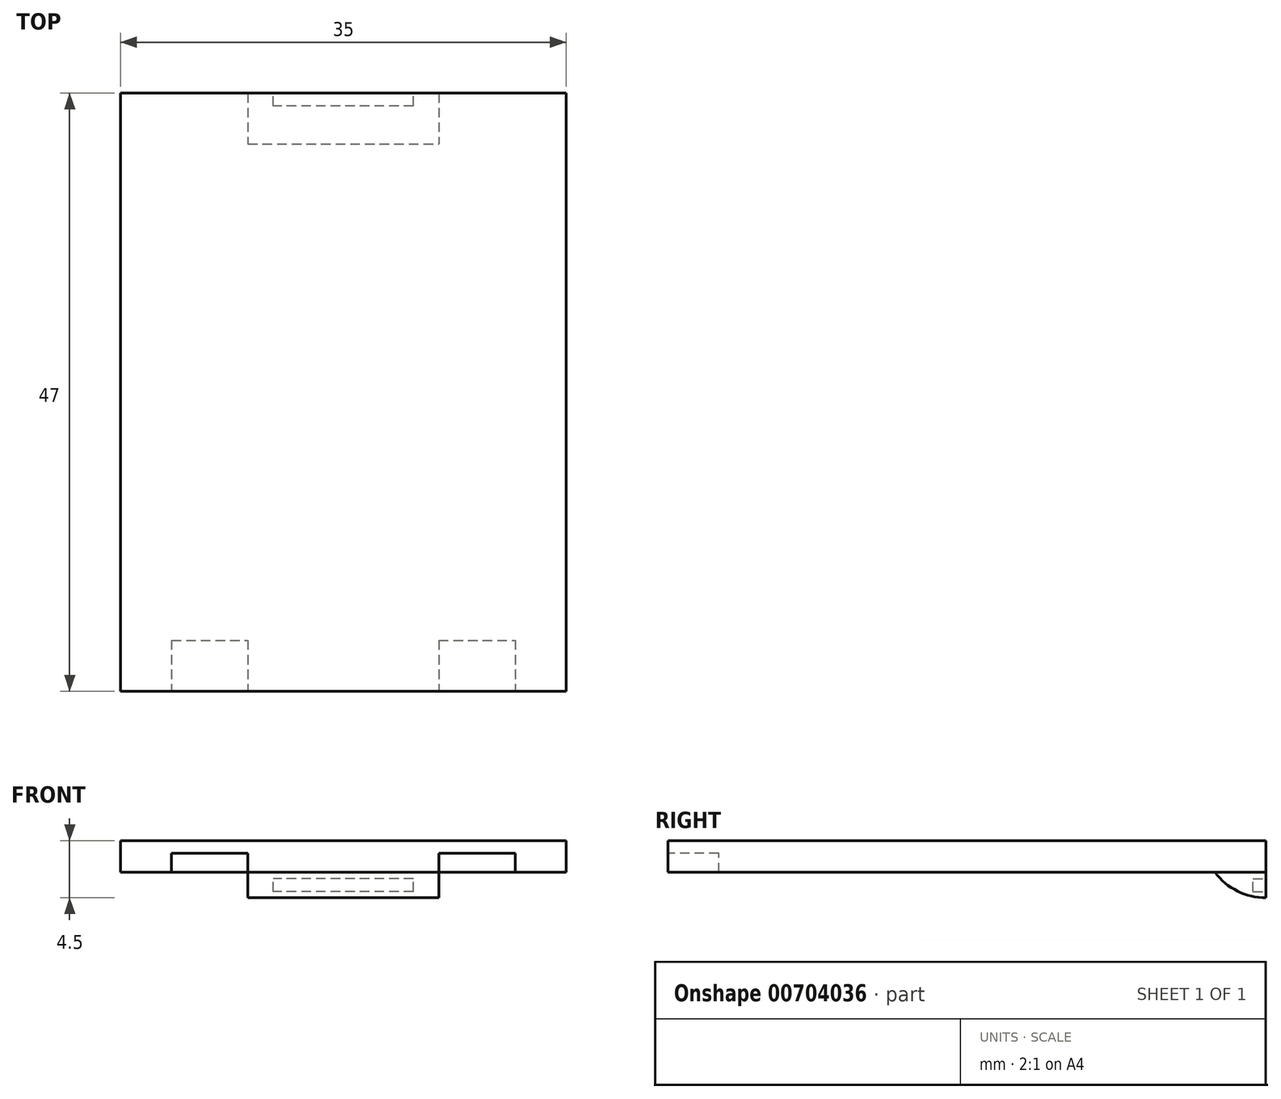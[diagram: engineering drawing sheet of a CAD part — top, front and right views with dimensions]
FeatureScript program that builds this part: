
annotation { "Feature Type Name" : "Feature", "Feature Type Description" : "" }
export const myFeature = defineFeature(function(context is Context, id is Id, definition is map)
    precondition{}
    {
        {
            var Q0;
            Q0=qCreatedBy(makeId("Top.planeOp"),FACE);
            var sketch = newSketch(context, id + "F0", { "sketchPlane" : qUnion([Q0])});
            skLineSegment(sketch, "E0.bottom", {"start": v(-10.93, 23.2) * mm, "end": v(24.07, 23.2) * mm});
            skLineSegment(sketch, "E0.top", {"start": v(-10.93, -23.8) * mm, "end": v(24.07, -23.8) * mm});
            skLineSegment(sketch, "E0.left", {"start": v(-10.93, 23.2) * mm, "end": v(-10.93, -23.8) * mm});
            skLineSegment(sketch, "E0.right", {"start": v(24.07, 23.2) * mm, "end": v(24.07, -23.8) * mm});
            skSolve(sketch);
        }
        {
            var Q0;
            Q0=makeQuery(id+"F0.imprint","IMPRINT",FACE,{"disambiguationData":[TD([[makeQuery(id+"F0.imprint","IMPRINT",EDGE,{"derivedFrom":sQuery(id+"F0.wireOp",EDGE,"E0.bottom")}),-1.0]])]});
            extrude(context, id + "F1", {"entities" : qUnion([Q0]), "depth" : 2.5 * mm, "offsetDistance" : 25 * mm});
        }
        {
            var Q0;
            Q0=makeQuery(id+"F1.opExtrude","SWEPT_FACE",FACE,{"disambiguationData":[OSD([sQuery(id+"F0.wireOp",EDGE,"E0.top")])]});
            var sketch = newSketch(context, id + "F2", { "sketchPlane" : qUnion([Q0])});
            skLineSegment(sketch, "E1.bottom", {"start": v(-6.93, 0) * mm, "end": v(-0.93, 0) * mm});
            skLineSegment(sketch, "E1.top", {"start": v(-6.93, 1.5) * mm, "end": v(-0.93, 1.5) * mm});
            skLineSegment(sketch, "E1.left", {"start": v(-6.93, 0) * mm, "end": v(-6.93, 1.5) * mm});
            skLineSegment(sketch, "E1.right", {"start": v(-0.93, 0) * mm, "end": v(-0.93, 1.5) * mm});
            skLineSegment(sketch, "E2.bottom", {"start": v(14.07, 0) * mm, "end": v(20.07, 0) * mm});
            skLineSegment(sketch, "E2.top", {"start": v(14.07, 1.5) * mm, "end": v(20.07, 1.5) * mm});
            skLineSegment(sketch, "E2.left", {"start": v(14.07, 0) * mm, "end": v(14.07, 1.5) * mm});
            skLineSegment(sketch, "E2.right", {"start": v(20.07, 0) * mm, "end": v(20.07, 1.5) * mm});
            skSolve(sketch);
        }
        {
            var Q0;
            Q0=makeQuery(id+"F2.imprint","IMPRINT",FACE,{"disambiguationData":[TD([[makeQuery(id+"F2.imprint","IMPRINT",EDGE,{"derivedFrom":sQuery(id+"F2.wireOp",EDGE,"E1.bottom")}),1.0]])]});
            var Q1;
            Q1=makeQuery(id+"F2.imprint","IMPRINT",FACE,{"disambiguationData":[TD([[makeQuery(id+"F2.imprint","IMPRINT",EDGE,{"derivedFrom":sQuery(id+"F2.wireOp",EDGE,"E2.bottom")}),1.0]])]});
            extrude(context, id + "F3", {"entities" : qUnion([Q0, Q1]), "operationType" : NewBodyOperationType.REMOVE, "oppositeDirection" : true, "depth" : 4 * mm, "offsetDistance" : 25 * mm});
        }
        {
            var Q0;
            Q0=makeQuery(id+"F1.opExtrude","CAP_FACE",FACE,{"disambiguationData":[OSD([sQuery(id+"F0.wireOp",EDGE,"E0.bottom"),sQuery(id+"F0.wireOp",EDGE,"E0.top"),sQuery(id+"F0.wireOp",EDGE,"E0.left"),sQuery(id+"F0.wireOp",EDGE,"E0.right")])],"isStart":true});
            var sketch = newSketch(context, id + "F4", { "sketchPlane" : qUnion([Q0])});
            skLineSegment(sketch, "E3.bottom", {"start": v(-0.93, -23.2) * mm, "end": v(14.07, -23.2) * mm});
            skLineSegment(sketch, "E3.top", {"start": v(-0.93, -19.2) * mm, "end": v(14.07, -19.2) * mm});
            skLineSegment(sketch, "E3.left", {"start": v(-0.93, -23.2) * mm, "end": v(-0.93, -19.2) * mm});
            skLineSegment(sketch, "E3.right", {"start": v(14.07, -23.2) * mm, "end": v(14.07, -19.2) * mm});
            skSolve(sketch);
        }
        {
            var Q0;
            Q0=makeQuery(id+"F4.imprint","IMPRINT",FACE,{"disambiguationData":[TD([[makeQuery(id+"F4.imprint","IMPRINT",EDGE,{"derivedFrom":sQuery(id+"F4.wireOp",EDGE,"E3.bottom")}),1.0]])]});
            extrude(context, id + "F5", {"entities" : qUnion([Q0]), "operationType" : NewBodyOperationType.ADD, "depth" : 2 * mm, "offsetDistance" : 25 * mm});
        }
        {
            var Q0;
            Q0=makeQuery(id+"F5.opExtrude","CAP_EDGE",EDGE,{"disambiguationData":[OSD([sQuery(id+"F4.wireOp",EDGE,"E3.top")])],"isStart":false});
            fillet(context, id + "F6", {"entities" : qUnion([Q0]), "radius" : 5 * mm, "tangentPropagation" : true, "allowEdgeOverflow" : false});
        }
        {
            var Q0;
            Q0=makeQuery(id+"F5.boolean.opBoolean","MERGE",FACE,{"derivedFrom":[makeQuery(id+"F1.opExtrude","SWEPT_FACE",FACE,{"disambiguationData":[OSD([sQuery(id+"F0.wireOp",EDGE,"E0.bottom")])]}),makeQuery(id+"F5.opExtrude","SWEPT_FACE",FACE,{"disambiguationData":[OSD([sQuery(id+"F4.wireOp",EDGE,"E3.bottom")])]})]});
            var sketch = newSketch(context, id + "F7", { "sketchPlane" : qUnion([Q0])});
            skLineSegment(sketch, "E4.bottom", {"start": v(-12.07, -1.5) * mm, "end": v(-1.07, -1.5) * mm});
            skLineSegment(sketch, "E4.top", {"start": v(-12.07, -0.5) * mm, "end": v(-1.07, -0.5) * mm});
            skLineSegment(sketch, "E4.left", {"start": v(-12.07, -1.5) * mm, "end": v(-12.07, -0.5) * mm});
            skLineSegment(sketch, "E4.right", {"start": v(-1.07, -1.5) * mm, "end": v(-1.07, -0.5) * mm});
            skSolve(sketch);
        }
        {
            var Q0;
            Q0=makeQuery(id+"F7.imprint","IMPRINT",FACE,{"disambiguationData":[TD([[makeQuery(id+"F7.imprint","IMPRINT",EDGE,{"derivedFrom":sQuery(id+"F7.wireOp",EDGE,"E4.bottom")}),1.0]])]});
            extrude(context, id + "F8", {"entities" : qUnion([Q0]), "operationType" : NewBodyOperationType.REMOVE, "oppositeDirection" : true, "depth" : 1 * mm, "offsetDistance" : 25 * mm});
        }
    });
